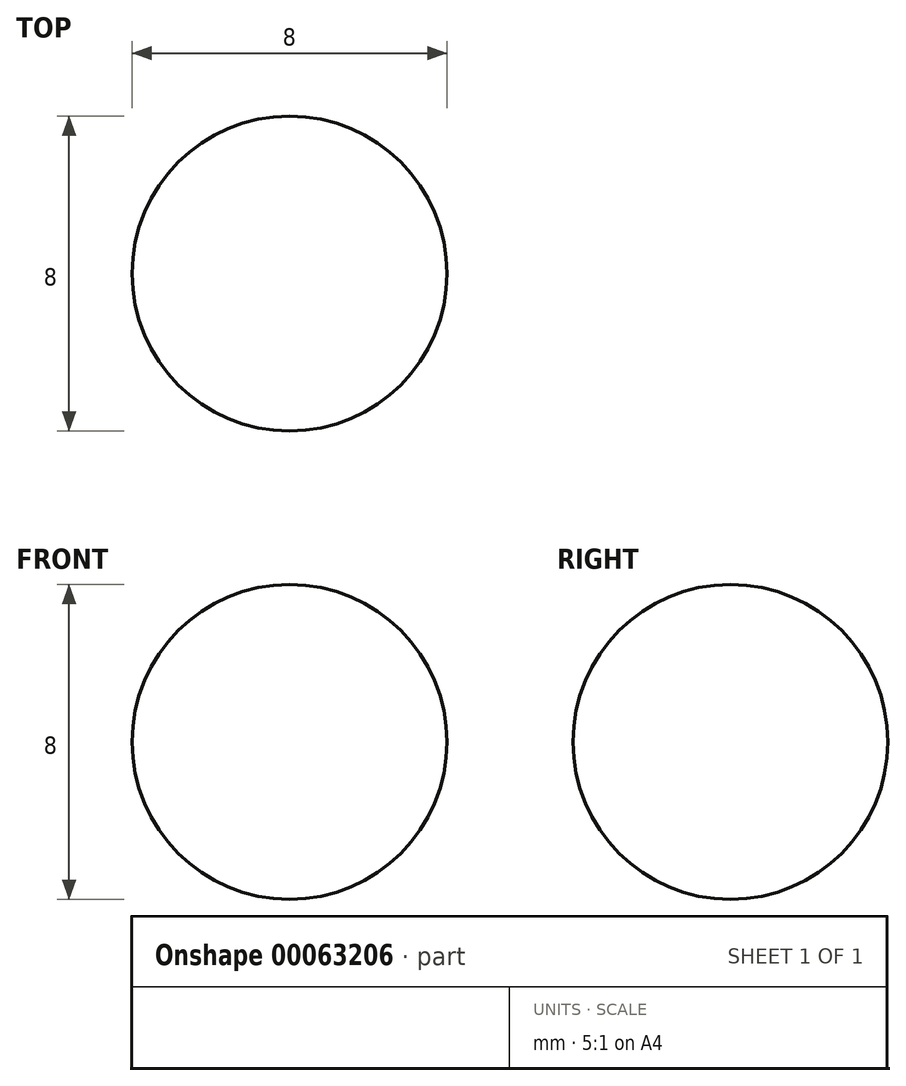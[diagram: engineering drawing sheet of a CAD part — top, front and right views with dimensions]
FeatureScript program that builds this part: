
annotation { "Feature Type Name" : "Feature", "Feature Type Description" : "" }
export const myFeature = defineFeature(function(context is Context, id is Id, definition is map)
    precondition{}
    {
        {
            var Q0;
            Q0=qCreatedBy(makeId("Front.planeOp"),FACE);
            var sketch = newSketch(context, id + "F0", { "sketchPlane" : qUnion([Q0])});
            skArc(sketch, "E0", {"start": v(0, 4) * mm, "mid": v(-4, 0) * mm, "end": v(0, -4) * mm});
            skLineSegment(sketch, "E1", {"start": v(0, 4) * mm, "end": v(0, -4) * mm});
            skSolve(sketch);
        }
        {
            var Q0;
            Q0=makeQuery(id+"F0.imprint","IMPRINT",FACE,{"disambiguationData":[TD([[makeQuery(id+"F0.imprint","IMPRINT",EDGE,{"derivedFrom":sQuery(id+"F0.wireOp",EDGE,"E0")}),1.0]])]});
            var Q1;
            Q1=sQuery(id+"F0.wireOp",EDGE,"E1");
            revolve(context, id + "F1", {"entities" : qUnion([Q0]), "axis" : qUnion([Q1]), "revolveType" : RevolveType.FULL});
        }
    });
